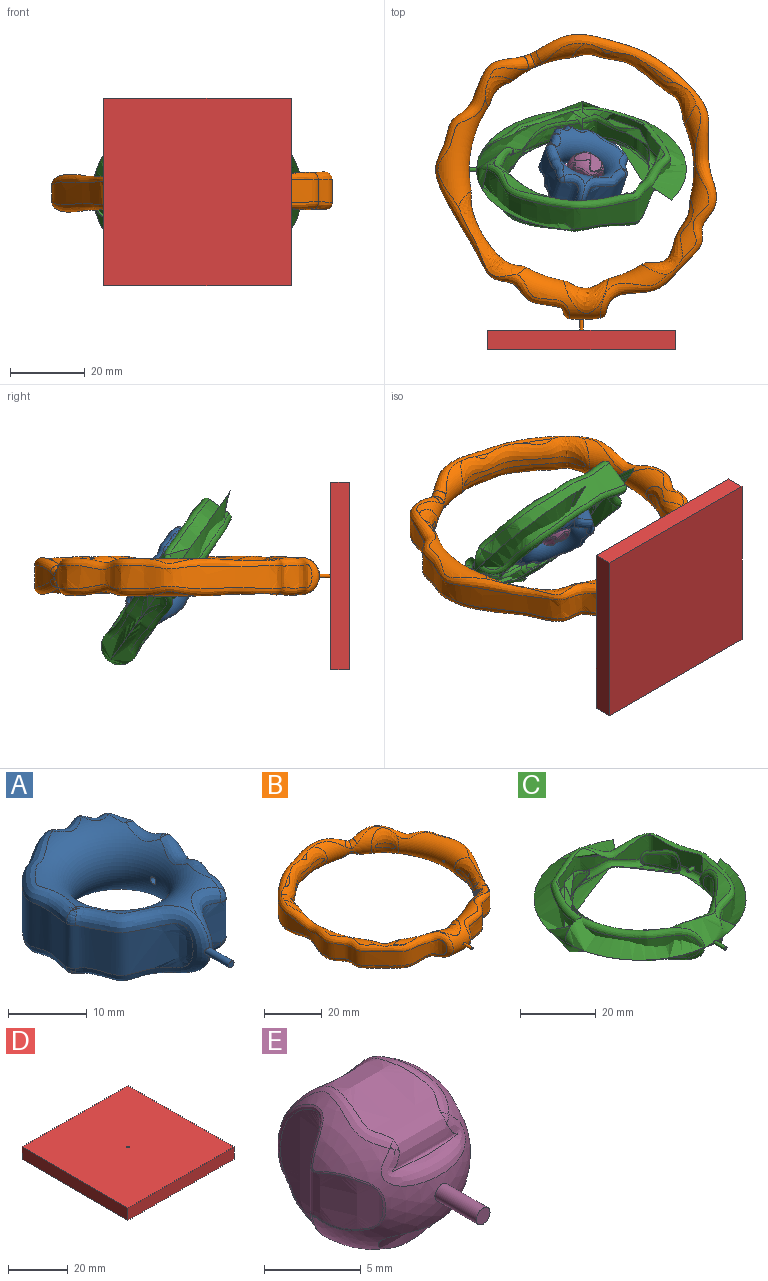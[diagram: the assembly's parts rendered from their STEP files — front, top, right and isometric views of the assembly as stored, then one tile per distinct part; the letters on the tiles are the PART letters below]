
ASSEMBLY  parts=5 mates=4
PART A: 40 faces, bbox 31.5x35.7x12.7 mm
  f0: torus R=11mm, axis (0,0,-1), area 627.3mm2, adj f1,f3,f23,f25,f26,f27,f28,f29
  f1: cylinder r=0.5mm len=2mm, axis (1,0,0), area 6.2mm2, adj f0,f2
  f2: plane 1x1mm, normal (-1,0,0), area 0.8mm2, adj f1
  f3: bspline ~13.8x4.83mm, area 42.2mm2, adj f0,f4,f21,f22
  f4: extruded ~27.48x22.57mm, area 508.1mm2, adj f3,f5,f6,f8,f10,f11,f12,f13
  f5: bspline ~1.58x1.34mm, area 0.7mm2, adj f4,f23,f25
  f6: bspline ~1.46x0.91mm, area 0.1mm2, adj f4,f7,f26
  f7: bspline ~1.62x1.5mm, area 1.8mm2, adj f6,f25,f26
  f8: bspline ~1.23x0.99mm, area 0.6mm2, adj f4,f9,f26
  f9: bspline ~1.96x1.79mm, area 1.6mm2, adj f8,f26,f27
  f10: bspline ~1.59x1.39mm, area 1.2mm2, adj f4,f27,f28
  f11: bspline ~1.89x1.61mm, area 1.5mm2, adj f4,f28,f39
  f12: bspline ~1.73x1.61mm, area 1.3mm2, adj f4,f29,f39
  f13: bspline ~1.59x1.39mm, area 1.2mm2, adj f4,f29,f31
  f14: bspline ~1.24x0.99mm, area 0.6mm2, adj f4,f15,f32
  f15: bspline ~1.96x1.79mm, area 1.6mm2, adj f14,f31,f32
  f16: bspline ~1.46x0.92mm, area 0.1mm2, adj f4,f17,f32
  f17: bspline ~1.62x1.5mm, area 1.8mm2, adj f16,f32,f33
  f18: bspline ~1.86x1.6mm, area 1.3mm2, adj f4,f33,f34
  f19: bspline ~2.33x1.6mm, area 1.5mm2, adj f4,f34,f35
  f20: bspline ~1.59x1.56mm, area 1.4mm2, adj f4,f35,f36
  f21: bspline ~2.33x1.6mm, area 1mm2, adj f3,f4,f23
  f22: bspline ~1.59x1.56mm, area 1.3mm2, adj f3,f4,f36
  f23: bspline ~5.51x3.62mm, area 16.3mm2, adj f0,f4,f5,f21,f24
  f24: bspline ~1.06x0.43mm, area 0mm2, adj f23,f25
  f25: bspline ~3.73x2.05mm, area 6.8mm2, adj f0,f4,f5,f7,f24
  f26: bspline ~4.21x3.18mm, area 8.6mm2, adj f0,f4,f6,f7,f8,f9
  f27: bspline ~6.34x3.31mm, area 12.9mm2, adj f0,f4,f9,f10
  f28: bspline ~15.44x11.51mm, area 55.2mm2, adj f0,f4,f10,f11
  f29: bspline ~15.41x11.51mm, area 55.9mm2, adj f0,f4,f12,f13,f30
  f30: bspline ~0.76x0.56mm, area 0mm2, adj f29,f39
  f31: bspline ~6.29x3.31mm, area 12.9mm2, adj f0,f4,f13,f15
  f32: bspline ~4.23x3.23mm, area 8.6mm2, adj f0,f4,f14,f15,f16,f17
  f33: bspline ~3.98x2.16mm, area 6.8mm2, adj f0,f4,f17,f18
  f34: bspline ~5.52x3.63mm, area 16.3mm2, adj f0,f4,f18,f19
  f35: bspline ~13.79x4.82mm, area 42.1mm2, adj f0,f4,f19,f20
  f36: bspline ~10x6.29mm, area 47.3mm2, adj f0,f4,f20,f22,f37,f39
  f37: cylinder r=0.5mm len=4.04mm, axis (0,1,0), area 12.7mm2, adj f36,f38,f39
  f38: plane 1x1mm, normal (0,-1,0), area 0.8mm2, adj f37
  f39: bspline ~13.89x11.77mm, area 106.5mm2, adj f0,f4,f11,f12,f30,f36,f37
PART B: 31 faces, bbox 83.5x85.7x71 mm
  f0: torus R=35mm, axis (0,0,-1), area 2.7mm2, adj f12,f27
  f1: torus R=35mm, axis (0,0,-1), area 7.2mm2, adj f12,f27
  f2: torus R=35mm, axis (0,0,-1), area 307.4mm2, adj f12,f26,f27
  f3: torus R=35mm, axis (0,0,-1), area 7.2mm2, adj f12,f27
  f4: torus R=35mm, axis (0,0,-1), area 2.7mm2, adj f12,f27
  f5: torus R=35mm, axis (0,0,-1), area 166.5mm2, adj f9,f10,f11,f12,f13,f20,f27,f28
  f6: torus R=35mm, axis (0,0,-1), area 460.3mm2, adj f7,f8,f12,f17,f20,f26,f29,f30
  f7: torus R=35mm, axis (0,0,-1), area 1.2mm2, adj f6,f12
  f8: torus R=35mm, axis (0,0,-1), area 0.2mm2, adj f6,f20
  f9: bspline ~35.09x4.87mm, area 10.6mm2, adj f5,f13,f19,f20
  f10: bspline ~4.06x3.49mm, area 10.6mm2, adj f5,f11,f19,f20
  f11: bspline ~35.18x5.04mm, area 11mm2, adj f5,f10,f12,f19
  f12: bspline ~75.81x51.5mm, area 865.1mm2, adj f0,f1,f2,f3,f4,f5,f6,f7
  f13: bspline ~35.18x5.04mm, area 11mm2, adj f5,f9,f12,f19
  f14: torus R=35mm, axis (0,0,-1), area 430.2mm2, adj f15,f20,f28,f29
  f15: cylinder r=0.5mm len=1.99mm, axis (1,0,0), area 6.2mm2, adj f14,f16
  f16: plane 1x1mm, normal (-1,0,0), area 0.8mm2, adj f15
  f17: cylinder r=0.5mm len=4.01mm, axis (0,1,0), area 12.6mm2, adj f6,f18
  f18: plane 1x1mm, normal (0,-1,0), area 0.8mm2, adj f17
  f19: extruded ~74.77x73.91mm, area 1475.6mm2, adj f9,f10,f11,f12,f13,f20
  f20: bspline ~69.71x35.82mm, area 577.5mm2, adj f5,f6,f8,f9,f10,f14,f19,f28
  f21: extruded ~16.32x10.89mm, area 71.1mm2, adj f26
  f22: extruded ~9.22x2mm, area 16.7mm2, adj f30
  f23: extruded ~18.72x12.95mm, area 37.9mm2, adj f29
  f24: extruded ~5.18x4.79mm, area 12.7mm2, adj f28
  f25: extruded ~28.84x17.45mm, area 64mm2, adj f27
  f26: bspline ~20.37x13.92mm, area 190.7mm2, adj f2,f6,f12,f21
  f27: bspline ~33.76x21.73mm, area 380.6mm2, adj f0,f1,f2,f3,f4,f5,f12,f25
  f28: bspline ~9.98x8.09mm, area 95.1mm2, adj f5,f14,f20,f24
  f29: bspline ~32.56x24.66mm, area 309.2mm2, adj f6,f14,f20,f23
  f30: bspline ~19.83x12.01mm, area 185.5mm2, adj f6,f22
PART C: 14 faces, bbox 60.6x62.3x22.4 mm
  f0: torus R=23mm, axis (0,0,-1), area 957mm2, adj f1,f3,f5,f7,f9,f13
  f1: cylinder r=0.5mm len=1.99mm, axis (1,0,0), area 6.2mm2, adj f0,f2
  f2: plane 1x1mm, normal (1,0,0), area 0.8mm2, adj f1
  f3: cylinder r=0.5mm len=4.02mm, axis (0,1,0), area 12.6mm2, adj f0,f4
  f4: plane 1x1mm, normal (0,1,0), area 0.8mm2, adj f3
  f5: bspline ~51.65x46.05mm, area 773mm2, adj f0,f6
  f6: extruded ~50.89x45.73mm, area 893mm2, adj f5
  f7: bspline ~9.94x6.68mm, area 29.1mm2, adj f0,f8
  f8: extruded ~8.72x4.81mm, area 35.9mm2, adj f7
  f9: bspline ~23.82x18.31mm, area 145.7mm2, adj f0,f10,f11,f12
  f10: extruded ~39.23x36.5mm, area 357.3mm2, adj f9,f11,f12,f13
  f11: bspline ~1.2x1.09mm, area 0.3mm2, adj f9,f10,f13
  f12: bspline ~1.2x1.09mm, area 0.3mm2, adj f9,f10,f13
  f13: bspline ~36.34x17.94mm, area 112.1mm2, adj f0,f10,f11,f12
PART D: 8 faces, bbox 50x50x5 mm
  f0: plane 50x5mm, normal (1,0,0), area 250mm2, adj f1,f3,f4,f5
  f1: plane 50x5mm, normal (0,1,0), area 250mm2, adj f0,f2,f4,f5
  f2: plane 50x5mm, normal (-1,0,0), area 250mm2, adj f1,f3,f4,f5
  f3: plane 50x5mm, normal (0,-1,0), area 250mm2, adj f0,f2,f4,f5
  f4: plane 50x50mm, normal (0,0,1), area 2499.2mm2, adj f0,f1,f2,f3,f6
  f5: plane 50x50mm, normal (0,0,-1), area 2500mm2, adj f0,f1,f2,f3
  f6: cylinder r=0.5mm len=1mm, axis (0,0,1), area 3.1mm2, adj f4,f7
  f7: plane 1x1mm, normal (0,0,1), area 0.8mm2, adj f6
PART E: 31 faces, bbox 9.6x13x10 mm
  f0: bspline ~5.11x1.81mm, area 1.6mm2, adj f1,f5,f26,f30
  f1: sphere r=5mm, area 85.4mm2, adj f0,f2,f4,f10,f11,f15,f17,f21
  f2: cylinder r=0.5mm len=3.03mm, axis (0,1,0), area 9.5mm2, adj f1,f3
  f3: plane 1x1mm, normal (0,-1,0), area 0.8mm2, adj f2
  f4: extruded ~5.58x2.12mm, area 13.7mm2, adj f1
  f5: extruded ~6.08x5.66mm, area 36.7mm2, adj f0,f25,f26,f29
  f6: extruded ~8.68x4.78mm, area 44.7mm2, adj f9,f10,f11,f12
  f7: extruded ~7.55x7.28mm, area 38.4mm2, adj f27,f28,f29,f30
  f8: extruded ~6.78x5.99mm, area 24.8mm2, adj f13,f15,f16,f17,f19,f21,f22,f24
  f9: bspline ~0.48x0.46mm, area 0.1mm2, adj f6,f10,f11
  f10: bspline ~5.95x1.97mm, area 8.4mm2, adj f1,f6,f9,f12
  f11: bspline ~8.31x5.98mm, area 14.1mm2, adj f1,f6,f9,f12
  f12: bspline ~0.48x0.46mm, area 0.1mm2, adj f6,f10,f11
  f13: bspline ~0.97x0.4mm, area 0.4mm2, adj f8,f14,f15
  f14: bspline ~0.93x0.77mm, area 0.4mm2, adj f13,f15,f17
  f15: bspline ~4.91x3.22mm, area 6.2mm2, adj f1,f8,f13,f14,f16,f18
  f16: bspline ~0.73x0.17mm, area 0mm2, adj f8,f15,f18
  f17: bspline ~5.59x2.52mm, area 7.1mm2, adj f1,f8,f14,f20
  f18: bspline ~0.31x0.22mm, area 0mm2, adj f15,f16,f21
  f19: bspline ~0.97x0.4mm, area 0.4mm2, adj f8,f20,f22
  f20: bspline ~0.93x0.77mm, area 0.4mm2, adj f17,f19,f22
  f21: bspline ~2.12x1.72mm, area 0.8mm2, adj f1,f8,f18,f23,f26
  f22: bspline ~4.84x2.95mm, area 6.3mm2, adj f1,f8,f19,f20,f23,f24
  f23: bspline ~0.31x0.22mm, area 0mm2, adj f21,f22,f24
  f24: bspline ~0.73x0.17mm, area 0mm2, adj f8,f22,f23
  f25: bspline ~6.26x5.81mm, area 3.8mm2, adj f1,f5,f26,f27
  f26: bspline ~0.67x0.59mm, area 0.2mm2, adj f0,f5,f21,f25
  f27: bspline ~0.43x0.36mm, area 0.1mm2, adj f7,f25,f28,f29
  f28: bspline ~7.95x7.72mm, area 6mm2, adj f1,f7,f27,f30
  f29: bspline ~2.01x1.35mm, area 0.7mm2, adj f5,f7,f27,f30
  f30: bspline ~0.49x0.42mm, area 0.1mm2, adj f0,f7,f28,f29
PLACE A rot(axis=(-0.07,-0.89,0.46),165.5deg) t=(55.24,25.93,40.57)mm
PLACE B rot(axis=(0,1,0),179.4deg) t=(55.24,25.93,40.57)mm
PLACE C rot(axis=(-0.41,-0.42,-0.81),102.4deg) t=(55.24,25.93,40.57)mm
PLACE D rot(axis=(-1,0,0),90deg) t=(55.24,-22.07,40.57)mm fixed
PLACE E rot(axis=(0.24,0.3,-0.92),111.2deg) t=(56.21,25.69,40.41)mm
MATE revolute C.f1 <-> A.f37  axis (0.01,0.58,-0.82) through (55.07,14.38,56.89)mm
MATE revolute E.f2 <-> A.f1  axis (-0.96,0.24,0.16) through (48.55,27.59,41.67)mm
MATE revolute B.f15 <-> C.f3  axis (1,0,0.01) through (23.24,25.93,40.24)mm
MATE revolute B.f17 <-> D.f6  axis (0,-1,0) through (55.24,-18.07,40.57)mm
